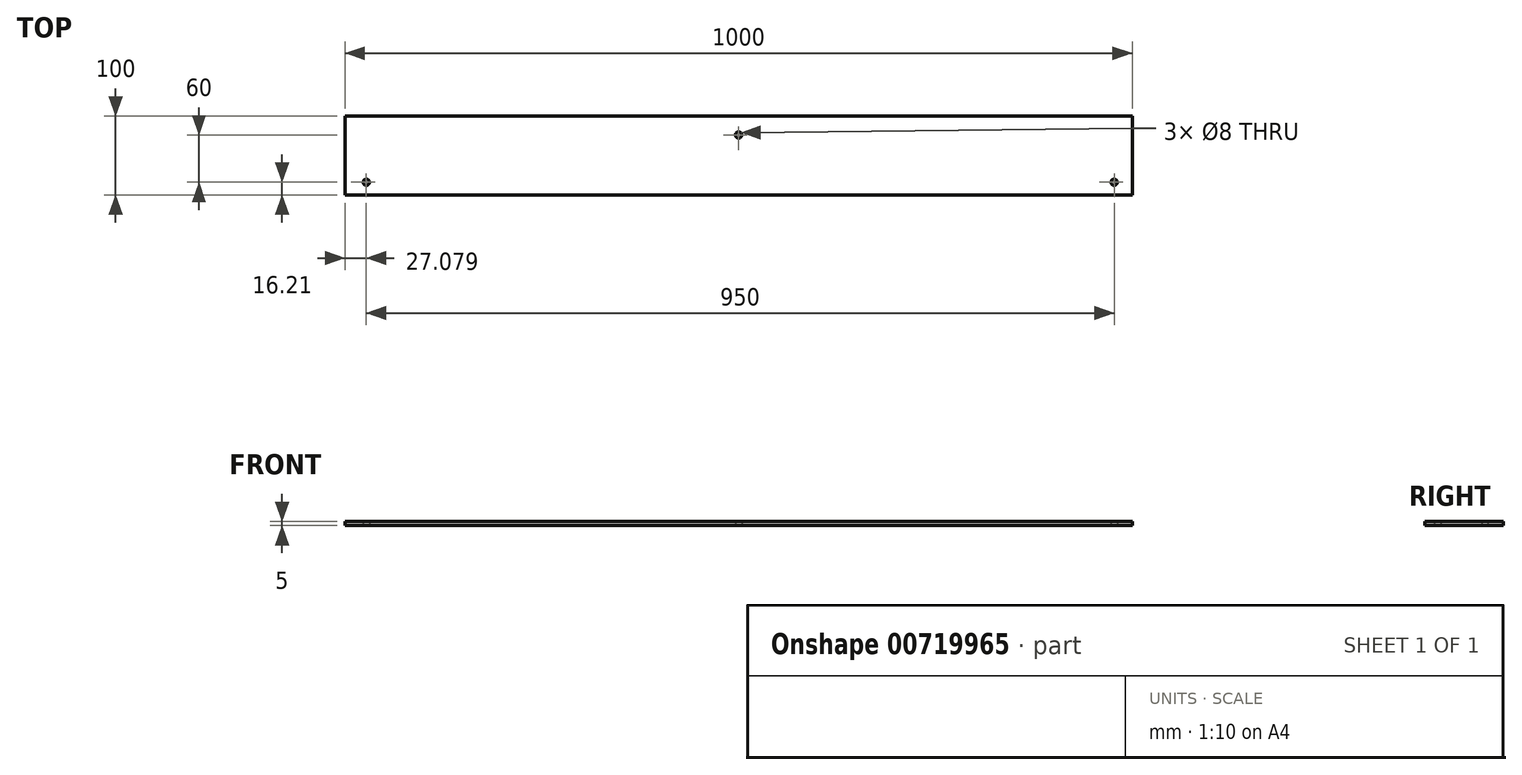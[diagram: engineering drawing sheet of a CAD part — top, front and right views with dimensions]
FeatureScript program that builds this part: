
annotation { "Feature Type Name" : "Feature", "Feature Type Description" : "" }
export const myFeature = defineFeature(function(context is Context, id is Id, definition is map)
    precondition{}
    {
        {
            var Q0;
            Q0=qCreatedBy(makeId("Top.planeOp"), FACE);
            var sketch = newSketch(context, id + "F0", { "sketchPlane" : qUnion([Q0])});
            skCircle(sketch, "E0", {"center": v(0, 60) * mm, "radius": 4 * mm});
            skCircle(sketch, "E1", {"center": v(-472.92, 0) * mm, "radius": 4 * mm});
            skCircle(sketch, "E2", {"center": v(477.08, 0) * mm, "radius": 4 * mm});
            skLineSegment(sketch, "E3.bottom", {"start": v(500, -16.2) * mm, "end": v(-500, -16.2) * mm});
            skLineSegment(sketch, "E3.top", {"start": v(500, 83.8) * mm, "end": v(-500, 83.8) * mm});
            skLineSegment(sketch, "E3.left", {"start": v(500, -16.2) * mm, "end": v(500, 83.8) * mm});
            skLineSegment(sketch, "E3.right", {"start": v(-500, -16.2) * mm, "end": v(-500, 83.8) * mm});
            skSolve(sketch);
        }
        {
            var Q0;
            Q0 = qSketchRegion(id + "F0", true);
            extrude(context, id + "F1", {"entities" : qUnion([Q0]), "depth" : 5 * mm, "offsetDistance" : 25 * mm});
        }
    });
